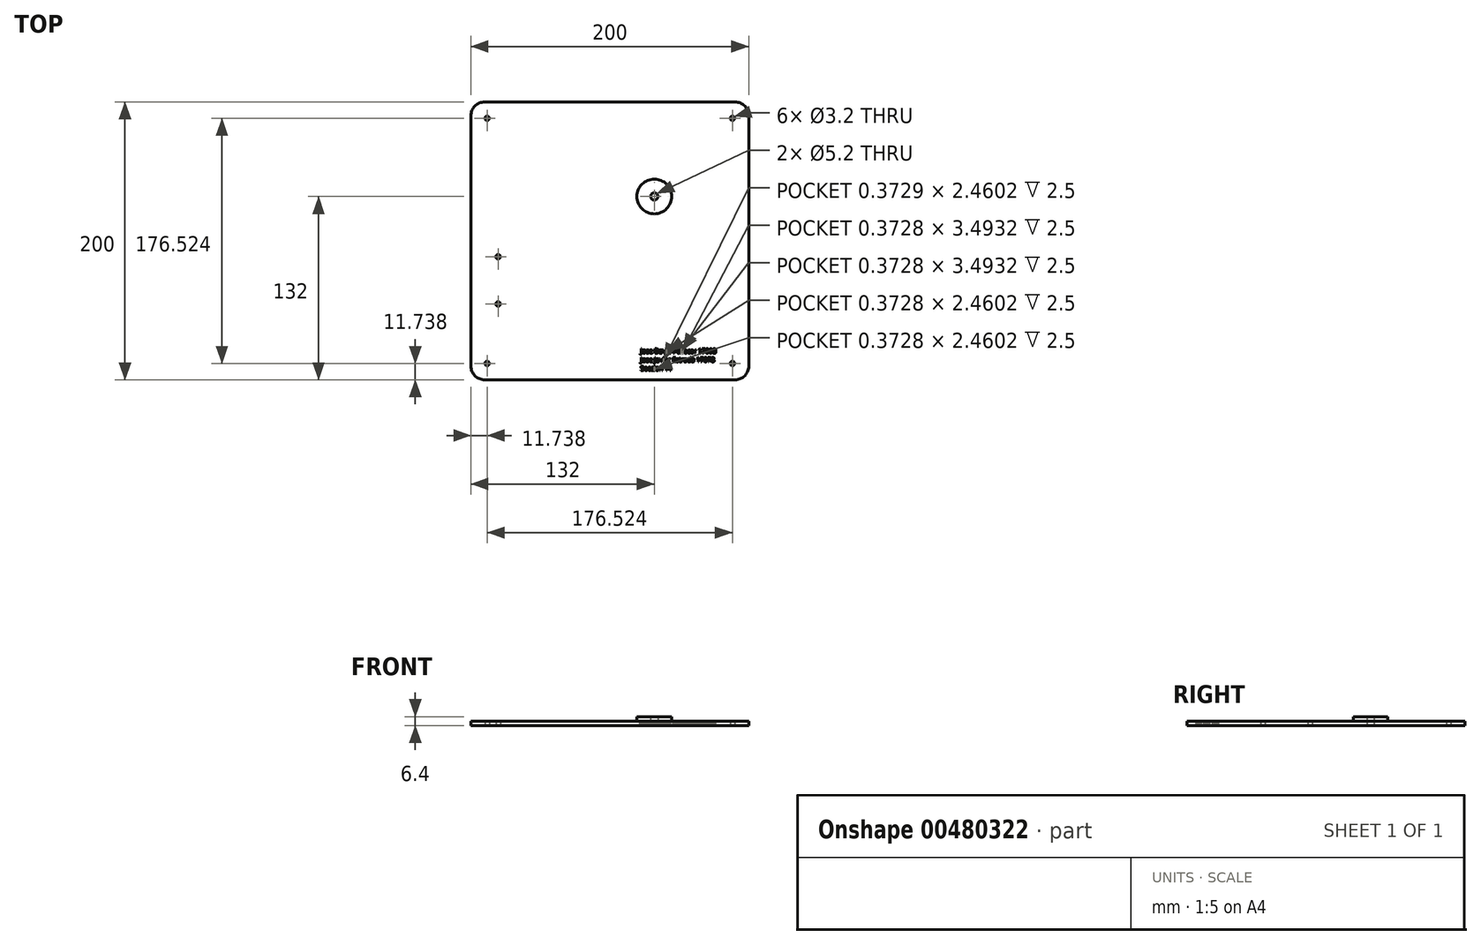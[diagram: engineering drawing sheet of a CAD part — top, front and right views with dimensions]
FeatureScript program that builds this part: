
annotation { "Feature Type Name" : "Feature", "Feature Type Description" : "" }
export const myFeature = defineFeature(function(context is Context, id is Id, definition is map)
    precondition{}
    {
        {
            var Q0;
            Q0=qCreatedBy(makeId("Top.planeOp"),FACE);
            var sketch = newSketch(context, id + "F0", { "sketchPlane" : qUnion([Q0])});
            skLineSegment(sketch, "E0.bottom", {"start": v(-100, 100) * mm, "end": v(100, 100) * mm});
            skLineSegment(sketch, "E0.top", {"start": v(-100, -100) * mm, "end": v(100, -100) * mm});
            skLineSegment(sketch, "E0.left", {"start": v(-100, 100) * mm, "end": v(-100, -100) * mm});
            skLineSegment(sketch, "E0.right", {"start": v(100, 100) * mm, "end": v(100, -100) * mm});
            skPoint(sketch, "E0.middle", {"position": v(0, 0) * mm});
            skLineSegment(sketch, "E1", {"start": v(-100, -100) * mm, "end": v(100, 100) * mm, "construction": true});
            skCircle(sketch, "E2", {"center": v(32, 32) * mm, "radius": 65 * mm, "construction": true});
            skCircle(sketch, "E3", {"center": v(32, 32) * mm, "radius": 2.6 * mm});
            skCircle(sketch, "E4", {"center": v(-80.4, -45.4) * mm, "radius": 1.6 * mm});
            skCircle(sketch, "E5.MirrorC", {"center": v(-80.4, -11.4) * mm, "radius": 1.6 * mm});
            skLineSegment(sketch, "E6", {"start": v(-100, 100) * mm, "end": v(100, -100) * mm, "construction": true});
            skCircle(sketch, "E7", {"center": v(88.26, -88.26) * mm, "radius": 1.6 * mm});
            skCircle(sketch, "E8", {"center": v(88.26, 88.26) * mm, "radius": 1.6 * mm});
            skCircle(sketch, "E9", {"center": v(-88.26, 88.26) * mm, "radius": 1.6 * mm});
            skCircle(sketch, "E10", {"center": v(-88.26, -88.26) * mm, "radius": 1.6 * mm});
            skSolve(sketch);
        }
        {
            var Q0;
            Q0=makeQuery(id+"F0.imprint","IMPRINT",FACE,{"disambiguationData":[TD([[makeQuery(id+"F0.imprint","IMPRINT",EDGE,{"derivedFrom":sQuery(id+"F0.wireOp",EDGE,"E0.bottom")}),-1.0]])]});
            extrude(context, id + "F1", {"entities" : qUnion([Q0]), "depth" : 3.2 * mm, "offsetDistance" : 25 * mm});
        }
        {
            var Q0;
            Q0=makeQuery(id+"F1.opExtrude","CAP_FACE",FACE,{"disambiguationData":[OSD([sQuery(id+"F0.wireOp",EDGE,"E0.bottom"),sQuery(id+"F0.wireOp",EDGE,"E0.top"),sQuery(id+"F0.wireOp",EDGE,"E0.left"),sQuery(id+"F0.wireOp",EDGE,"E0.right"),sQuery(id+"F0.wireOp",EDGE,"E3")])],"isStart":false});
            var sketch = newSketch(context, id + "F2", { "sketchPlane" : qUnion([Q0])});
            skText(sketch, "E11", { "text": "Jose David Pellecer 17003\nJose Javier Estrada 17078\nSeccion 11", "fontName": "OpenSans-Regular.ttf"});
            const initialGuessF2  = {"E11": [0.02207, -0.0809, 1, 0, 0.00331]};
            skSetInitialGuess(sketch, initialGuessF2);
            skSolve(sketch);
        }
        {
            var Q0;
            Q0 = qSketchRegion(id + "F2", true);
            extrude(context, id + "F3", {"entities" : qUnion([Q0]), "operationType" : NewBodyOperationType.REMOVE, "oppositeDirection" : true, "depth" : 2.5 * mm, "offsetDistance" : 25 * mm});
        }
        {
            var Q0;
            {var subQ0=sQuery(id+"F0.wireOp",EDGE,"E0.bottom");var subQ1=sQuery(id+"F0.wireOp",EDGE,"E0.top");var subQ2=sQuery(id+"F0.wireOp",EDGE,"E0.right");var subQ3=sQuery(id+"F0.wireOp",EDGE,"E3");var subQ4=sQuery(id+"F0.wireOp",EDGE,"E4");var subQ5=sQuery(id+"F0.wireOp",EDGE,"E5.MirrorC");var subQ6=sQuery(id+"F0.wireOp",EDGE,"E0.left");Q0=makeQuery(id+"F3.boolean.opBoolean","SPLIT",FACE,{"disambiguationData":[TD([makeQuery(id+"F1.opExtrude","SWEPT_FACE",FACE,{"disambiguationData":[OSD([subQ0])]})])],"derivedFrom":makeQuery(id+"F1.opExtrude","CAP_FACE",FACE,{"disambiguationData":[OSD([subQ0,subQ1,subQ6,subQ2,subQ3,subQ4,subQ5])],"isStart":false})});}
            var sketch = newSketch(context, id + "F4", { "sketchPlane" : qUnion([Q0])});
            skCircle(sketch, "E12.0", {"center": v(32, 32) * mm, "radius": 2.6 * mm});
            skCircle(sketch, "E13", {"center": v(32, 32) * mm, "radius": 12.5 * mm});
            skSolve(sketch);
        }
        {
            var Q0;
            Q0 = qSketchRegion(id + "F4", true);
            var Q1;
            Q1=makeQuery(id+"F4.imprint","IMPRINT",FACE,{"disambiguationData":[TD([[makeQuery(id+"F4.imprint","IMPRINT",EDGE,{"derivedFrom":sQuery(id+"F4.wireOp",EDGE,"E12.0")}),-1.0]])]});
            extrude(context, id + "F5", {"entities" : qUnion([Q0, Q1]), "depth" : 3.2 * mm, "offsetDistance" : 25 * mm});
        }
        {
            var Q0;
            Q0=makeQuery(id+"F1.opExtrude","SWEPT_EDGE",EDGE,{"disambiguationData":[OSD([sQuery(id+"F0.wireOp",EDGE,"E0.bottom"),sQuery(id+"F0.wireOp",EDGE,"E0.right")])]});
            var Q1;
            Q1=makeQuery(id+"F1.opExtrude","SWEPT_EDGE",EDGE,{"disambiguationData":[OSD([sQuery(id+"F0.wireOp",EDGE,"E0.bottom"),sQuery(id+"F0.wireOp",EDGE,"E0.left")])]});
            var Q2;
            Q2=makeQuery(id+"F1.opExtrude","SWEPT_EDGE",EDGE,{"disambiguationData":[OSD([sQuery(id+"F0.wireOp",EDGE,"E0.top"),sQuery(id+"F0.wireOp",EDGE,"E0.left")])]});
            var Q3;
            Q3=makeQuery(id+"F1.opExtrude","SWEPT_EDGE",EDGE,{"disambiguationData":[OSD([sQuery(id+"F0.wireOp",EDGE,"E0.top"),sQuery(id+"F0.wireOp",EDGE,"E0.right")])]});
            fillet(context, id + "F6", {"entities" : qUnion([Q0, Q1, Q2, Q3]), "radius" : 10 * mm, "tangentPropagation" : true, "allowEdgeOverflow" : false});
        }
    });
